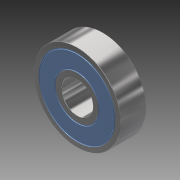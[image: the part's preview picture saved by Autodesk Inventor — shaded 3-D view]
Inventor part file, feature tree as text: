
AUTODESK INVENTOR PART (.ipt)
format: ipt  version: 2016 SP1 (Build 200210100, 210)  size: 181,248 bytes
history: native  units: in
note: dims shown in document units (in); Inventor stores cm internally (conversion verified against a paired STEP export)
features: sketch x2, extrude x1, fillet x1, revolve x1, plane x1, mirror x1
ambient origin geometry x8: Origin, YZ Plane, XZ Plane, XY Plane, X Axis, Y Axis, Z Axis, Center Point
bodies: Solid1 (feature_tree)
feature tree (7):
  extrude  "Extrusion1"  Depth=0.5512in
  fillet  "Fillet1"  Radius=0.5512in
  revolve  "Revolution1"  Angle=90.0deg
  plane  "Work Plane1"
  mirror  "Mirror1"
  sketch  "Sketch1"  dims[d0=0.6693in d1=1.8504in d2=0.5512in d3=0.0in]
  sketch  "Sketch2"  dims[d4=0.0118in d5=90.0deg]
